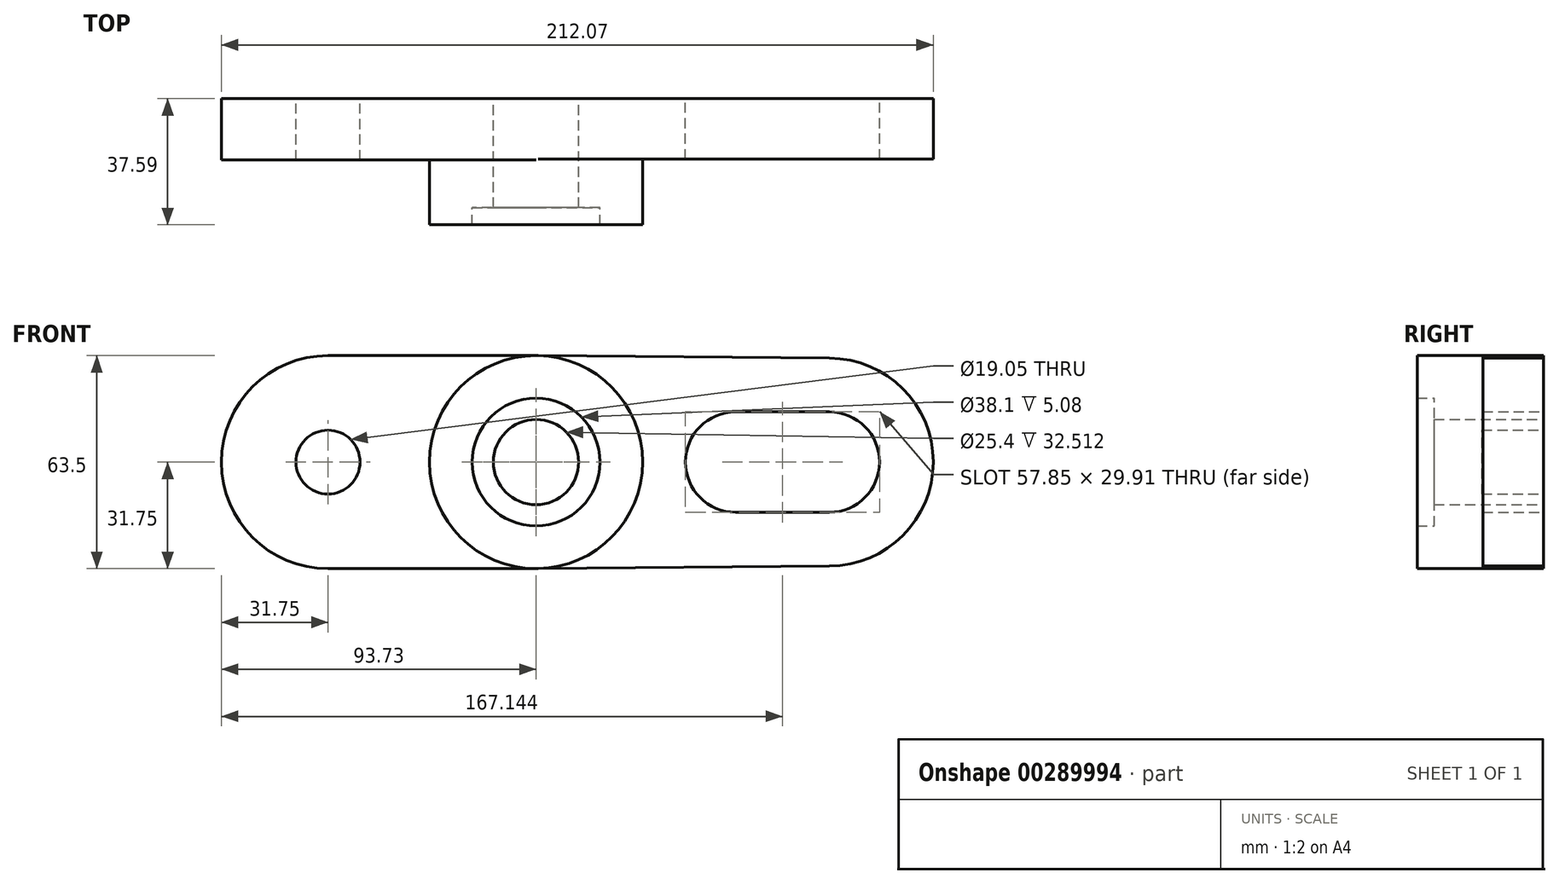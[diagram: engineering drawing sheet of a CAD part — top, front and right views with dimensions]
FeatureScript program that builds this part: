
annotation { "Feature Type Name" : "Feature", "Feature Type Description" : "" }
export const myFeature = defineFeature(function(context is Context, id is Id, definition is map)
    precondition{}
    {
        {
            var Q0;
            Q0=qCreatedBy(makeId("Front.planeOp"),FACE);
            var sketch = newSketch(context, id + "F0", { "sketchPlane" : qUnion([Q0])});
            skCircle(sketch, "E0", {"center": v(0, 0) * mm, "radius": 31.75 * mm});
            skCircle(sketch, "E1", {"center": v(0, 0) * mm, "radius": 12.7 * mm});
            skCircle(sketch, "E2", {"center": v(0, 0) * mm, "radius": 19.05 * mm});
            skPoint(sketch, "E3", {"position": v(87.38, 0) * mm});
            skPoint(sketch, "E4", {"position": v(59.44, 0) * mm});
            skArc(sketch, "E5", {"start": v(59.44, 14.95) * mm, "mid": v(44.5, 0) * mm, "end": v(59.44, -14.95) * mm});
            skArc(sketch, "E6", {"start": v(87.38, -14.95) * mm, "mid": v(102.34, 0) * mm, "end": v(87.38, 14.95) * mm});
            skPoint(sketch, "E7", {"position": v(59.44, 14.95) * mm});
            skPoint(sketch, "E8", {"position": v(87.38, 14.95) * mm});
            skPoint(sketch, "E9", {"position": v(87.38, -14.95) * mm});
            skPoint(sketch, "E10", {"position": v(59.44, -14.95) * mm});
            skLineSegment(sketch, "E11", {"start": v(59.44, 14.95) * mm, "end": v(87.38, 14.95) * mm});
            skLineSegment(sketch, "E12", {"start": v(59.44, -14.95) * mm, "end": v(87.38, -14.95) * mm});
            skArc(sketch, "E13", {"start": v(87.38, -30.95) * mm, "mid": v(118.34, 0) * mm, "end": v(87.38, 30.95) * mm});
            skPoint(sketch, "E14", {"position": v(118.34, 0) * mm});
            skPoint(sketch, "E14.positionSnap0", {"position": v(102.34, 0) * mm});
            skPoint(sketch, "E15", {"position": v(87.38, 30.95) * mm});
            skPoint(sketch, "E16", {"position": v(87.38, -30.95) * mm});
            skPoint(sketch, "E17", {"position": v(0, 31.75) * mm});
            skPoint(sketch, "E18", {"position": v(0, -31.75) * mm});
            skLineSegment(sketch, "E19", {"start": v(0, 31.75) * mm, "end": v(87.38, 30.95) * mm});
            skLineSegment(sketch, "E20", {"start": v(0, -31.75) * mm, "end": v(87.38, -30.95) * mm});
            skPoint(sketch, "E21", {"position": v(-61.98, 0) * mm});
            skCircle(sketch, "E22", {"center": v(-61.98, 0) * mm, "radius": 9.53 * mm});
            skArc(sketch, "E23", {"start": v(-61.98, 31.75) * mm, "mid": v(-93.73, 0) * mm, "end": v(-61.98, -31.75) * mm});
            skPoint(sketch, "E24", {"position": v(-61.98, 31.75) * mm});
            skPoint(sketch, "E25", {"position": v(-61.98, -31.75) * mm});
            skLineSegment(sketch, "E26", {"start": v(-61.98, 31.75) * mm, "end": v(0, 31.75) * mm});
            skLineSegment(sketch, "E27", {"start": v(-61.98, -31.75) * mm, "end": v(0, -31.75) * mm});
            skPoint(sketch, "E28", {"position": v(-93.73, 0) * mm});
            skSolve(sketch);
        }
        {
            var Q0;
            Q0=makeQuery(id+"F0.imprint","IMPRINT",FACE,{"disambiguationData":[TD([[makeQuery(id+"F0.imprint","IMPRINT",EDGE,{"derivedFrom":sQuery(id+"F0.wireOp",EDGE,"E22")}),-1.0]])]});
            extrude(context, id + "F1", {"entities" : qUnion([Q0]), "depth" : 18.29 * mm});
        }
        {
            var Q0;
            Q0=makeQuery(id+"F0.imprint","IMPRINT",FACE,{"disambiguationData":[TD([[makeQuery(id+"F0.imprint","IMPRINT",EDGE,{"derivedFrom":sQuery(id+"F0.wireOp",EDGE,"E2")}),-1.0]])]});
            extrude(context, id + "F2", {"entities" : qUnion([Q0]), "operationType" : NewBodyOperationType.ADD, "depth" : 37.6 * mm});
        }
        {
            var Q0;
            Q0=makeQuery(id+"F0.imprint","IMPRINT",FACE,{"disambiguationData":[TD([[makeQuery(id+"F0.imprint","IMPRINT",EDGE,{"derivedFrom":sQuery(id+"F0.wireOp",EDGE,"E5")}),-1.0]])]});
            extrude(context, id + "F3", {"entities" : qUnion([Q0]), "operationType" : NewBodyOperationType.ADD, "depth" : 18.03 * mm});
        }
        {
            var Q0;
            Q0=sQuery(id+"F0.wireOp",EDGE,"E1");
            extrude(context, id + "F4", {"bodyType" : ToolBodyType.SURFACE, "surfaceEntities" : qUnion([Q0]), "depth" : 27.43 * mm});
        }
        {
            var Q0;
            Q0=makeQuery(id+"F0.imprint","IMPRINT",FACE,{"disambiguationData":[TD([[makeQuery(id+"F0.imprint","IMPRINT",EDGE,{"derivedFrom":sQuery(id+"F0.wireOp",EDGE,"E1")}),-1.0]])]});
            extrude(context, id + "F5", {"entities" : qUnion([Q0]), "operationType" : NewBodyOperationType.ADD, "depth" : 32.5 * mm});
        }
    });
